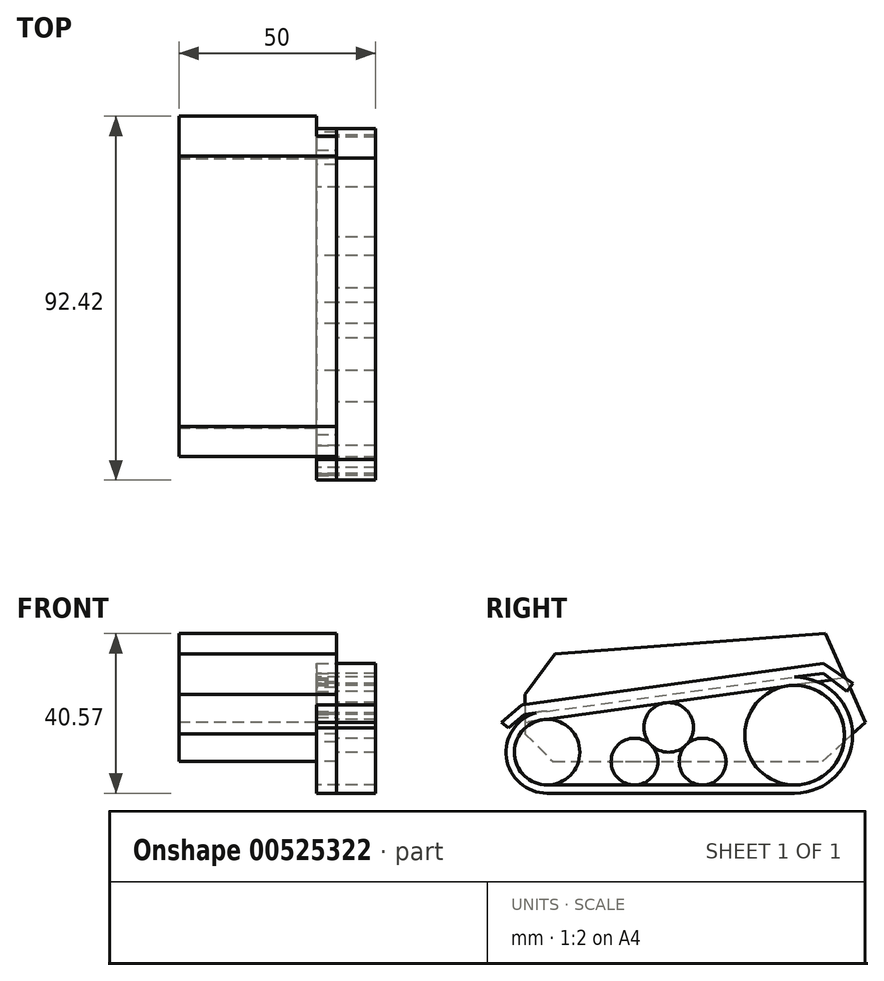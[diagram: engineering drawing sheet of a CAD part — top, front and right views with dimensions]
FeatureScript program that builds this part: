
annotation { "Feature Type Name" : "Feature", "Feature Type Description" : "" }
export const myFeature = defineFeature(function(context is Context, id is Id, definition is map)
    precondition{}
    {
        {
            var Q0;
            Q0=qCreatedBy(makeId("Right.planeOp"),FACE);
            var sketch = newSketch(context, id + "F0", { "sketchPlane" : qUnion([Q0])});
            skLineSegment(sketch, "E0", {"start": v(38.57, 0) * mm, "end": v(28.4, 22.53) * mm});
            skLineSegment(sketch, "E1", {"start": v(28.4, 22.53) * mm, "end": v(-40.26, 17.4) * mm});
            skLineSegment(sketch, "E2", {"start": v(-40.26, 17.4) * mm, "end": v(-47.88, 7.07) * mm});
            skLineSegment(sketch, "E3", {"start": v(-47.88, 7.07) * mm, "end": v(-47.88, -2.93) * mm});
            skLineSegment(sketch, "E4", {"start": v(-47.88, -2.93) * mm, "end": v(-40.8, -10) * mm});
            skLineSegment(sketch, "E5", {"start": v(-40.8, -10) * mm, "end": v(27.7, -10) * mm});
            skLineSegment(sketch, "E6", {"start": v(27.7, -10) * mm, "end": v(38.57, 0) * mm});
            skSolve(sketch);
        }
        {
            var Q0;
            Q0=makeQuery(id+"F0.imprint","IMPRINT",FACE,{"disambiguationData":[TD([[makeQuery(id+"F0.imprint","IMPRINT",EDGE,{"derivedFrom":sQuery(id+"F0.wireOp",EDGE,"E0")}),1.0]])]});
            extrude(context, id + "F1", {"entities" : qUnion([Q0]), "depth" : 40 * mm, "offsetDistance" : 25 * mm});
        }
        {
            var Q0;
            Q0=makeQuery(id+"F1.opExtrude","CAP_FACE",FACE,{"disambiguationData":[OSD([sQuery(id+"F0.wireOp",EDGE,"E0"),sQuery(id+"F0.wireOp",EDGE,"E1"),sQuery(id+"F0.wireOp",EDGE,"E2"),sQuery(id+"F0.wireOp",EDGE,"E3"),sQuery(id+"F0.wireOp",EDGE,"E4"),sQuery(id+"F0.wireOp",EDGE,"E5"),sQuery(id+"F0.wireOp",EDGE,"E6")])],"isStart":false});
            var sketch = newSketch(context, id + "F2", { "sketchPlane" : qUnion([Q0])});
            skLineSegment(sketch, "E7", {"start": v(33.49, 11.27) * mm, "end": v(-49.63, -0.24) * mm, "construction": true});
            skCircle(sketch, "E8", {"center": v(20.6, -3.3) * mm, "radius": 12.65 * mm});
            skPoint(sketch, "E8.first.point", {"position": v(18.86, 9.24) * mm});
            skPoint(sketch, "E8.second.point", {"position": v(9.86, -10) * mm});
            skPoint(sketch, "E8.third.point", {"position": v(33.13, -5) * mm});
            skLineSegment(sketch, "E9", {"start": v(43.72, -15.95) * mm, "end": v(-53.78, -15.95) * mm, "construction": true});
            skCircle(sketch, "E10", {"center": v(-42.3, -7.63) * mm, "radius": 8.32 * mm});
            skPoint(sketch, "E10.first.point", {"position": v(-43.43, 0.62) * mm});
            skPoint(sketch, "E10.second.point", {"position": v(-42.3, -15.95) * mm});
            skPoint(sketch, "E10.third.point", {"position": v(-34.32, -10) * mm});
            skArc(sketch, "E11", {"start": v(20.6, 11.45) * mm, "mid": v(35.34, -3.3) * mm, "end": v(20.6, -18.04) * mm});
            skCircle(sketch, "E12.0", {"center": v(-42.3, -7.63) * mm, "radius": 10.41 * mm, "construction": true});
            skPoint(sketch, "E13.orphan", {"position": v(-47.88, 0) * mm});
            skLineSegment(sketch, "E14", {"start": v(-42.3, -7.63) * mm, "end": v(-42.3, 10.08) * mm, "construction": true});
            skLineSegment(sketch, "E15", {"start": v(20.6, -3.3) * mm, "end": v(20.6, 14.74) * mm, "construction": true});
            skArc(sketch, "E16", {"start": v(-42.3, 2.78) * mm, "mid": v(-52.7, -7.63) * mm, "end": v(-42.3, -18.04) * mm});
            skLineSegment(sketch, "E17", {"start": v(-42.3, -18.04) * mm, "end": v(20.6, -18.04) * mm});
            skLineSegment(sketch, "E18", {"start": v(-48.03, 2) * mm, "end": v(20.6, 11.45) * mm});
            skArc(sketch, "E19", {"start": v(-43.43, 0.62) * mm, "mid": v(-50.6, -8.2) * mm, "end": v(-42.3, -15.95) * mm});
            skArc(sketch, "E20", {"start": v(20.6, -15.95) * mm, "mid": v(33.22, -2.42) * mm, "end": v(18.86, 9.24) * mm});
            skLineSegment(sketch, "E21", {"start": v(-43.43, 0.62) * mm, "end": v(18.86, 9.24) * mm});
            skLineSegment(sketch, "E22", {"start": v(-42.3, -15.95) * mm, "end": v(20.6, -15.95) * mm});
            skCircle(sketch, "E23", {"center": v(-20.06, -10) * mm, "radius": 5.95 * mm});
            skCircle(sketch, "E24", {"center": v(-2.78, -10) * mm, "radius": 5.95 * mm});
            skCircle(sketch, "E25", {"center": v(-11.42, -1.32) * mm, "radius": 6.3 * mm});
            skPoint(sketch, "E25.first.point", {"position": v(-15.87, -5.78) * mm});
            skPoint(sketch, "E25.second.point", {"position": v(-6.98, -5.78) * mm});
            skPoint(sketch, "E25.third.point", {"position": v(-12.29, 4.93) * mm});
            skLineSegment(sketch, "E26.0", {"start": v(-48.62, 4.44) * mm, "end": v(27.91, 14.98) * mm});
            skLineSegment(sketch, "E27", {"start": v(-48.62, 4.44) * mm, "end": v(-53.85, 0) * mm});
            skLineSegment(sketch, "E28", {"start": v(-48.03, 2) * mm, "end": v(-52.12, -1.5) * mm});
            skLineSegment(sketch, "E29", {"start": v(-52.12, -1.5) * mm, "end": v(-53.85, 0) * mm});
            skLineSegment(sketch, "E30", {"start": v(20.6, 11.45) * mm, "end": v(27.91, 12.43) * mm});
            skLineSegment(sketch, "E31", {"start": v(27.91, 12.43) * mm, "end": v(33.85, 7.83) * mm});
            skLineSegment(sketch, "E32", {"start": v(33.85, 7.83) * mm, "end": v(35.41, 9.85) * mm});
            skLineSegment(sketch, "E33", {"start": v(27.91, 14.98) * mm, "end": v(35.41, 9.85) * mm});
            skSolve(sketch);
        }
        {
            var Q0;
            {var subQ5=sQuery(id+"F2.wireOp",EDGE,"E30");Q0=makeQuery(id+"F2.imprint","IMPRINT",FACE,{"disambiguationData":[TD([[makeQuery(id+"F2.imprint","IMPRINT",EDGE,{"derivedFrom":subQ5}),1.0]])]});}
            var Q1;
            {var subQ0=sQuery(id+"F2.wireOp",EDGE,"E18");var subQ3=sQuery(id+"F2.wireOp",EDGE,"E16");var subQ5=makeQuery(id+"F2.imprint","INTERSECT",VERTEX,{"disambiguationData":[OD(1.0)],"derivedFrom":[subQ3,subQ0]});Q1=makeQuery(id+"F2.imprint","IMPRINT",FACE,{"disambiguationData":[TD([[makeQuery(id+"F2.imprint","IMPRINT",EDGE,{"disambiguationData":[TD([[subQ5,-1.0]])],"derivedFrom":subQ3}),1.0]])]});}
            var Q2;
            {var subQ0=sQuery(id+"F2.wireOp",EDGE,"E17");Q2=makeQuery(id+"F2.imprint","IMPRINT",FACE,{"disambiguationData":[TD([[makeQuery(id+"F2.imprint","IMPRINT",EDGE,{"derivedFrom":subQ0}),1.0]])]});}
            var Q3;
            {var subQ1=sQuery(id+"F2.wireOp",EDGE,"E27");Q3=makeQuery(id+"F2.imprint","IMPRINT",FACE,{"disambiguationData":[TD([[makeQuery(id+"F2.imprint","IMPRINT",EDGE,{"derivedFrom":subQ1}),1.0]])]});}
            var Q4;
            {var subQ0=sQuery(id+"F2.wireOp",EDGE,"E33");var subQ1=sQuery(id+"F2.wireOp",EDGE,"E32");var subQ2=makeQuery(id+"F2.imprint","INTERSECT",VERTEX,{"derivedFrom":[subQ1,subQ0]});Q4=makeQuery(id+"F2.imprint","IMPRINT",FACE,{"disambiguationData":[TD([[makeQuery(id+"F2.imprint","IMPRINT",EDGE,{"disambiguationData":[TD([[subQ2,1.0]])],"derivedFrom":subQ1}),1.0]])]});}
            var Q5;
            {var subQ0=sQuery(id+"F2.wireOp",EDGE,"E25");var subQ1=makeQuery(id+"F2.imprint","INTERSECT",VERTEX,{"derivedFrom":[sQuery(id+"F2.wireOp",EDGE,"E21"),subQ0]});Q5=makeQuery(id+"F2.imprint","IMPRINT",FACE,{"disambiguationData":[TD([[makeQuery(id+"F2.imprint","IMPRINT",EDGE,{"disambiguationData":[TD([[subQ1,-1.0]])],"derivedFrom":subQ0}),1.0]])]});}
            var Q6;
            {var subQ0=sQuery(id+"F2.wireOp",EDGE,"E24");var subQ1=makeQuery(id+"F2.imprint","INTERSECT",VERTEX,{"derivedFrom":[sQuery(id+"F2.wireOp",EDGE,"E22"),subQ0]});Q6=makeQuery(id+"F2.imprint","IMPRINT",FACE,{"disambiguationData":[TD([[makeQuery(id+"F2.imprint","IMPRINT",EDGE,{"disambiguationData":[TD([[subQ1,1.0]])],"derivedFrom":subQ0}),1.0]])]});}
            var Q7;
            {var subQ0=sQuery(id+"F2.wireOp",EDGE,"E23");var subQ1=makeQuery(id+"F2.imprint","INTERSECT",VERTEX,{"derivedFrom":[sQuery(id+"F2.wireOp",EDGE,"E22"),subQ0]});Q7=makeQuery(id+"F2.imprint","IMPRINT",FACE,{"disambiguationData":[TD([[makeQuery(id+"F2.imprint","IMPRINT",EDGE,{"disambiguationData":[TD([[subQ1,1.0]])],"derivedFrom":subQ0}),1.0]])]});}
            var Q8;
            {var subQ0=sQuery(id+"F2.wireOp",EDGE,"E24");var subQ1=makeQuery(id+"F2.imprint","INTERSECT",VERTEX,{"derivedFrom":[subQ0,sQuery(id+"F2.wireOp",EDGE,"E25")]});Q8=makeQuery(id+"F2.imprint","IMPRINT",FACE,{"disambiguationData":[TD([[makeQuery(id+"F2.imprint","IMPRINT",EDGE,{"disambiguationData":[TD([[subQ1,1.0]])],"derivedFrom":subQ0}),1.0]])]});}
            var Q9;
            {var subQ0=sQuery(id+"F2.wireOp",EDGE,"E23");var subQ1=makeQuery(id+"F2.imprint","INTERSECT",VERTEX,{"derivedFrom":[subQ0,sQuery(id+"F2.wireOp",EDGE,"E25")]});Q9=makeQuery(id+"F2.imprint","IMPRINT",FACE,{"disambiguationData":[TD([[makeQuery(id+"F2.imprint","IMPRINT",EDGE,{"disambiguationData":[TD([[subQ1,1.0]])],"derivedFrom":subQ0}),1.0]])]});}
            var Q10;
            {var subQ0=sQuery(id+"F2.wireOp",EDGE,"E18");var subQ1=sQuery(id+"F2.wireOp",EDGE,"E16");var subQ2=makeQuery(id+"F2.imprint","INTERSECT",VERTEX,{"disambiguationData":[OD(0.0)],"derivedFrom":[subQ1,subQ0]});Q10=makeQuery(id+"F2.imprint","IMPRINT",FACE,{"disambiguationData":[TD([[makeQuery(id+"F2.imprint","IMPRINT",EDGE,{"disambiguationData":[TD([[subQ2,-1.0]])],"derivedFrom":subQ1}),1.0]])]});}
            extrude(context, id + "F3", {"entities" : qUnion([Q0, Q1, Q2, Q3, Q4, Q5, Q6, Q7, Q8, Q9, Q10]), "depth" : 10 * mm, "offsetDistance" : 25 * mm, "hasSecondDirection" : true, "secondDirectionOppositeDirection" : true, "secondDirectionDepth" : 5 * mm});
        }
        {
            var Q0;
            {var subQ8=makeQuery(id+"F1.opExtrude","CAP_EDGE",EDGE,{"disambiguationData":[OSD([sQuery(id+"F0.wireOp",EDGE,"E1")])],"isStart":false});Q0=makeQuery(id+"F2.imprint","IMPRINT",FACE,{"disambiguationData":[TD([[makeQuery(id+"F2.imprint","IMPRINT",EDGE,{"derivedFrom":subQ8}),1.0]])]});}
            var sketch = newSketch(context, id + "F4", { "sketchPlane" : qUnion([Q0])});
            skLineSegment(sketch, "E34.0", {"start": v(33.49, 11.27) * mm, "end": v(-49.63, -0.24) * mm});
            skLineSegment(sketch, "E35.0", {"start": v(38.57, 0) * mm, "end": v(28.4, 22.53) * mm});
            skLineSegment(sketch, "E36.0", {"start": v(27.7, -10) * mm, "end": v(38.57, 0) * mm});
            skLineSegment(sketch, "E37.0", {"start": v(-40.8, -10) * mm, "end": v(27.7, -10) * mm});
            skLineSegment(sketch, "E38.0", {"start": v(-47.88, -2.93) * mm, "end": v(-40.8, -10) * mm});
            skLineSegment(sketch, "E39.0", {"start": v(-47.88, 7.07) * mm, "end": v(-47.88, -2.93) * mm});
            skSolve(sketch);
        }
        {
            var Q0;
            {var subQ0=sQuery(id+"F4.wireOp",EDGE,"E36.0");Q0=makeQuery(id+"F4.imprint","IMPRINT",FACE,{"disambiguationData":[TD([[makeQuery(id+"F4.imprint","IMPRINT",EDGE,{"derivedFrom":subQ0}),1.0]])]});}
            extrude(context, id + "F5", {"entities" : qUnion([Q0]), "operationType" : NewBodyOperationType.REMOVE, "oppositeDirection" : true, "depth" : 5 * mm, "offsetDistance" : 25 * mm});
        }
        {
            var Q0;
            {var subQ0=makeQuery(id+"F1.opExtrude","CAP_EDGE",EDGE,{"disambiguationData":[OSD([sQuery(id+"F0.wireOp",EDGE,"E4")])],"isStart":false});Q0=makeQuery(id+"F2.imprint","IMPRINT",FACE,{"disambiguationData":[TD([[makeQuery(id+"F2.imprint","IMPRINT",EDGE,{"derivedFrom":subQ0}),1.0]])]});}
            var Q1;
            {var subQ0=makeQuery(id+"F1.opExtrude","CAP_EDGE",EDGE,{"disambiguationData":[OSD([sQuery(id+"F0.wireOp",EDGE,"E4")])],"isStart":false});Q1=makeQuery(id+"F2.imprint","IMPRINT",FACE,{"disambiguationData":[TD([[makeQuery(id+"F2.imprint","IMPRINT",EDGE,{"derivedFrom":subQ0}),-1.0]])]});}
            var Q2;
            {var subQ0=sQuery(id+"F2.wireOp",EDGE,"E8");var subQ1=makeQuery(id+"F2.imprint","INTERSECT",VERTEX,{"derivedFrom":[subQ0,sQuery(id+"F2.wireOp",EDGE,"E22")]});Q2=makeQuery(id+"F2.imprint","IMPRINT",FACE,{"disambiguationData":[TD([[makeQuery(id+"F2.imprint","IMPRINT",EDGE,{"disambiguationData":[TD([[subQ1,1.0]])],"derivedFrom":subQ0}),1.0]])]});}
            var Q3;
            {var subQ0=sQuery(id+"F2.wireOp",EDGE,"E8");var subQ1=makeQuery(id+"F2.imprint","INTERSECT",VERTEX,{"derivedFrom":[subQ0,sQuery(id+"F2.wireOp",EDGE,"E21")]});Q3=makeQuery(id+"F2.imprint","IMPRINT",FACE,{"disambiguationData":[TD([[makeQuery(id+"F2.imprint","IMPRINT",EDGE,{"disambiguationData":[TD([[subQ1,-1.0]])],"derivedFrom":subQ0}),1.0]])]});}
            extrude(context, id + "F6", {"entities" : qUnion([Q0, Q1, Q2, Q3]), "depth" : 10 * mm, "offsetDistance" : 25 * mm});
        }
        {
            var Q0;
            {var subQ1=sQuery(id+"F2.wireOp",EDGE,"E21");var subQ5=sQuery(id+"F2.wireOp",EDGE,"E8");var subQ6=makeQuery(id+"F2.imprint","INTERSECT",VERTEX,{"derivedFrom":[subQ5,subQ1]});Q0=makeQuery(id+"F2.imprint","IMPRINT",FACE,{"disambiguationData":[TD([[makeQuery(id+"F2.imprint","IMPRINT",EDGE,{"disambiguationData":[TD([[subQ6,-1.0]])],"derivedFrom":subQ5}),-1.0]])]});}
            var Q1;
            {var subQ0=sQuery(id+"F2.wireOp",EDGE,"E8");var subQ1=makeQuery(id+"F2.imprint","INTERSECT",VERTEX,{"derivedFrom":[subQ0,sQuery(id+"F2.wireOp",EDGE,"E21")]});Q1=makeQuery(id+"F2.imprint","IMPRINT",FACE,{"disambiguationData":[TD([[makeQuery(id+"F2.imprint","IMPRINT",EDGE,{"disambiguationData":[TD([[subQ1,-1.0]])],"derivedFrom":subQ0}),1.0]])]});}
            var Q2;
            {var subQ0=sQuery(id+"F2.wireOp",EDGE,"E8");var subQ1=makeQuery(id+"F2.imprint","INTERSECT",VERTEX,{"derivedFrom":[subQ0,sQuery(id+"F2.wireOp",EDGE,"E22")]});Q2=makeQuery(id+"F2.imprint","IMPRINT",FACE,{"disambiguationData":[TD([[makeQuery(id+"F2.imprint","IMPRINT",EDGE,{"disambiguationData":[TD([[subQ1,1.0]])],"derivedFrom":subQ0}),1.0]])]});}
            var Q3;
            {var subQ0=sQuery(id+"F2.wireOp",EDGE,"E22");var subQ1=sQuery(id+"F2.wireOp",EDGE,"E8");var subQ2=makeQuery(id+"F2.imprint","INTERSECT",VERTEX,{"derivedFrom":[subQ1,subQ0]});Q3=makeQuery(id+"F2.imprint","IMPRINT",FACE,{"disambiguationData":[TD([[makeQuery(id+"F2.imprint","IMPRINT",EDGE,{"disambiguationData":[TD([[subQ2,1.0]])],"derivedFrom":subQ1}),-1.0]])]});}
            var Q4;
            {var subQ0=sQuery(id+"F2.wireOp",EDGE,"E24");var subQ1=makeQuery(id+"F2.imprint","INTERSECT",VERTEX,{"derivedFrom":[sQuery(id+"F2.wireOp",EDGE,"E22"),subQ0]});Q4=makeQuery(id+"F2.imprint","IMPRINT",FACE,{"disambiguationData":[TD([[makeQuery(id+"F2.imprint","IMPRINT",EDGE,{"disambiguationData":[TD([[subQ1,1.0]])],"derivedFrom":subQ0}),1.0]])]});}
            var Q5;
            {var subQ0=sQuery(id+"F2.wireOp",EDGE,"E24");var subQ1=makeQuery(id+"F2.imprint","INTERSECT",VERTEX,{"derivedFrom":[subQ0,sQuery(id+"F2.wireOp",EDGE,"E25")]});Q5=makeQuery(id+"F2.imprint","IMPRINT",FACE,{"disambiguationData":[TD([[makeQuery(id+"F2.imprint","IMPRINT",EDGE,{"disambiguationData":[TD([[subQ1,1.0]])],"derivedFrom":subQ0}),1.0]])]});}
            var Q6;
            {var subQ0=sQuery(id+"F2.wireOp",EDGE,"E23");var subQ1=sQuery(id+"F2.wireOp",EDGE,"E22");var subQ2=makeQuery(id+"F2.imprint","INTERSECT",VERTEX,{"derivedFrom":[subQ1,subQ0]});Q6=makeQuery(id+"F2.imprint","IMPRINT",FACE,{"disambiguationData":[TD([[makeQuery(id+"F2.imprint","IMPRINT",EDGE,{"disambiguationData":[TD([[subQ2,-1.0]])],"derivedFrom":subQ1}),1.0]])]});}
            var Q7;
            {var subQ0=sQuery(id+"F2.wireOp",EDGE,"E25");var subQ1=sQuery(id+"F2.wireOp",EDGE,"E23");var subQ2=makeQuery(id+"F2.imprint","INTERSECT",VERTEX,{"derivedFrom":[subQ1,subQ0]});Q7=makeQuery(id+"F2.imprint","IMPRINT",FACE,{"disambiguationData":[TD([[makeQuery(id+"F2.imprint","IMPRINT",EDGE,{"disambiguationData":[TD([[subQ2,1.0]])],"derivedFrom":subQ1}),-1.0]])]});}
            var Q8;
            {var subQ0=sQuery(id+"F2.wireOp",EDGE,"E25");var subQ1=makeQuery(id+"F2.imprint","INTERSECT",VERTEX,{"derivedFrom":[sQuery(id+"F2.wireOp",EDGE,"E21"),subQ0]});Q8=makeQuery(id+"F2.imprint","IMPRINT",FACE,{"disambiguationData":[TD([[makeQuery(id+"F2.imprint","IMPRINT",EDGE,{"disambiguationData":[TD([[subQ1,-1.0]])],"derivedFrom":subQ0}),1.0]])]});}
            var Q9;
            {var subQ0=sQuery(id+"F2.wireOp",EDGE,"E23");var subQ1=makeQuery(id+"F2.imprint","INTERSECT",VERTEX,{"derivedFrom":[sQuery(id+"F2.wireOp",EDGE,"E22"),subQ0]});Q9=makeQuery(id+"F2.imprint","IMPRINT",FACE,{"disambiguationData":[TD([[makeQuery(id+"F2.imprint","IMPRINT",EDGE,{"disambiguationData":[TD([[subQ1,1.0]])],"derivedFrom":subQ0}),1.0]])]});}
            var Q10;
            {var subQ0=sQuery(id+"F2.wireOp",EDGE,"E23");var subQ1=makeQuery(id+"F2.imprint","INTERSECT",VERTEX,{"derivedFrom":[subQ0,sQuery(id+"F2.wireOp",EDGE,"E25")]});Q10=makeQuery(id+"F2.imprint","IMPRINT",FACE,{"disambiguationData":[TD([[makeQuery(id+"F2.imprint","IMPRINT",EDGE,{"disambiguationData":[TD([[subQ1,1.0]])],"derivedFrom":subQ0}),1.0]])]});}
            var Q11;
            {var subQ1=sQuery(id+"F2.wireOp",EDGE,"E21");var subQ7=sQuery(id+"F2.wireOp",EDGE,"E10");var subQ8=makeQuery(id+"F2.imprint","INTERSECT",VERTEX,{"derivedFrom":[subQ7,subQ1]});Q11=makeQuery(id+"F2.imprint","IMPRINT",FACE,{"disambiguationData":[TD([[makeQuery(id+"F2.imprint","IMPRINT",EDGE,{"disambiguationData":[TD([[subQ8,1.0]])],"derivedFrom":subQ7}),-1.0]])]});}
            var Q12;
            {var subQ0=sQuery(id+"F2.wireOp",EDGE,"E22");var subQ1=sQuery(id+"F2.wireOp",EDGE,"E10");var subQ2=makeQuery(id+"F2.imprint","INTERSECT",VERTEX,{"derivedFrom":[subQ1,subQ0]});Q12=makeQuery(id+"F2.imprint","IMPRINT",FACE,{"disambiguationData":[TD([[makeQuery(id+"F2.imprint","IMPRINT",EDGE,{"disambiguationData":[TD([[subQ2,-1.0]])],"derivedFrom":subQ1}),-1.0]])]});}
            var Q13;
            {var subQ0=makeQuery(id+"F1.opExtrude","CAP_EDGE",EDGE,{"disambiguationData":[OSD([sQuery(id+"F0.wireOp",EDGE,"E4")])],"isStart":false});Q13=makeQuery(id+"F2.imprint","IMPRINT",FACE,{"disambiguationData":[TD([[makeQuery(id+"F2.imprint","IMPRINT",EDGE,{"derivedFrom":subQ0}),-1.0]])]});}
            var Q14;
            {var subQ0=makeQuery(id+"F1.opExtrude","CAP_EDGE",EDGE,{"disambiguationData":[OSD([sQuery(id+"F0.wireOp",EDGE,"E4")])],"isStart":false});Q14=makeQuery(id+"F2.imprint","IMPRINT",FACE,{"disambiguationData":[TD([[makeQuery(id+"F2.imprint","IMPRINT",EDGE,{"derivedFrom":subQ0}),1.0]])]});}
            var Q15;
            {var subQ0=sQuery(id+"F2.wireOp",EDGE,"E17");Q15=makeQuery(id+"F2.imprint","IMPRINT",FACE,{"disambiguationData":[TD([[makeQuery(id+"F2.imprint","IMPRINT",EDGE,{"derivedFrom":subQ0}),1.0]])]});}
            var Q16;
            {var subQ5=sQuery(id+"F2.wireOp",EDGE,"E21");var subQ13=sQuery(id+"F2.wireOp",EDGE,"E8");var subQ14=makeQuery(id+"F2.imprint","INTERSECT",VERTEX,{"derivedFrom":[subQ13,subQ5]});Q16=makeQuery(id+"F2.imprint","IMPRINT",FACE,{"disambiguationData":[TD([[makeQuery(id+"F2.imprint","IMPRINT",EDGE,{"disambiguationData":[TD([[subQ14,1.0]])],"derivedFrom":subQ13}),-1.0]])]});}
            var Q17;
            {var subQ0=sQuery(id+"F2.wireOp",EDGE,"E30");Q17=makeQuery(id+"F2.imprint","IMPRINT",FACE,{"disambiguationData":[TD([[makeQuery(id+"F2.imprint","IMPRINT",EDGE,{"derivedFrom":subQ0}),1.0]])]});}
            var Q18;
            {var subQ1=sQuery(id+"F2.wireOp",EDGE,"E27");Q18=makeQuery(id+"F2.imprint","IMPRINT",FACE,{"disambiguationData":[TD([[makeQuery(id+"F2.imprint","IMPRINT",EDGE,{"derivedFrom":subQ1}),1.0]])]});}
            var Q19;
            {var subQ0=sQuery(id+"F2.wireOp",EDGE,"E33");var subQ1=sQuery(id+"F2.wireOp",EDGE,"E32");var subQ2=makeQuery(id+"F2.imprint","INTERSECT",VERTEX,{"derivedFrom":[subQ1,subQ0]});Q19=makeQuery(id+"F2.imprint","IMPRINT",FACE,{"disambiguationData":[TD([[makeQuery(id+"F2.imprint","IMPRINT",EDGE,{"disambiguationData":[TD([[subQ2,1.0]])],"derivedFrom":subQ1}),1.0]])]});}
            extrude(context, id + "F7", {"entities" : qUnion([Q0, Q1, Q2, Q3, Q4, Q5, Q6, Q7, Q8, Q9, Q10, Q11, Q12, Q13, Q14, Q15, Q16, Q17, Q18, Q19]), "oppositeDirection" : true, "depth" : 5 * mm, "offsetDistance" : 25 * mm});
        }
    });
